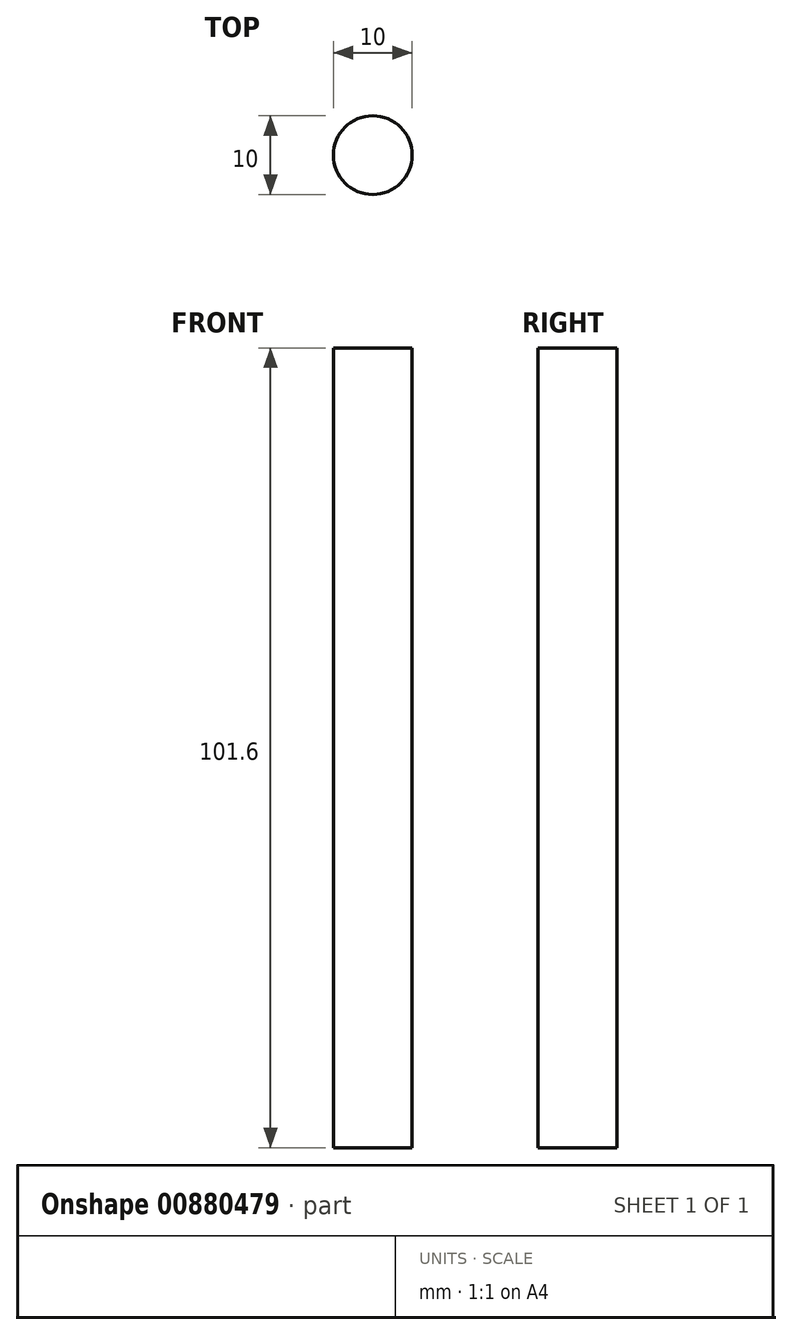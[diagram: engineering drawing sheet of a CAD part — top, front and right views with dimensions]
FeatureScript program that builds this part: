
annotation { "Feature Type Name" : "Feature", "Feature Type Description" : "" }
export const myFeature = defineFeature(function(context is Context, id is Id, definition is map)
    precondition{}
    {
        {
            var Q0;
            Q0=qCreatedBy(makeId("Top.planeOp"),FACE);
            var sketch = newSketch(context, id + "F0", { "sketchPlane" : qUnion([Q0])});
            skCircle(sketch, "E0", {"center": v(0, 0) * mm, "radius": 5 * mm});
            skSolve(sketch);
        }
        {
            var Q0;
            Q0 = qSketchRegion(id + "F0", true);
            extrude(context, id + "F1", {"entities" : qUnion([Q0]), "depth" : 101.6 * mm, "offsetDistance" : 25.4 * mm});
        }
    });
